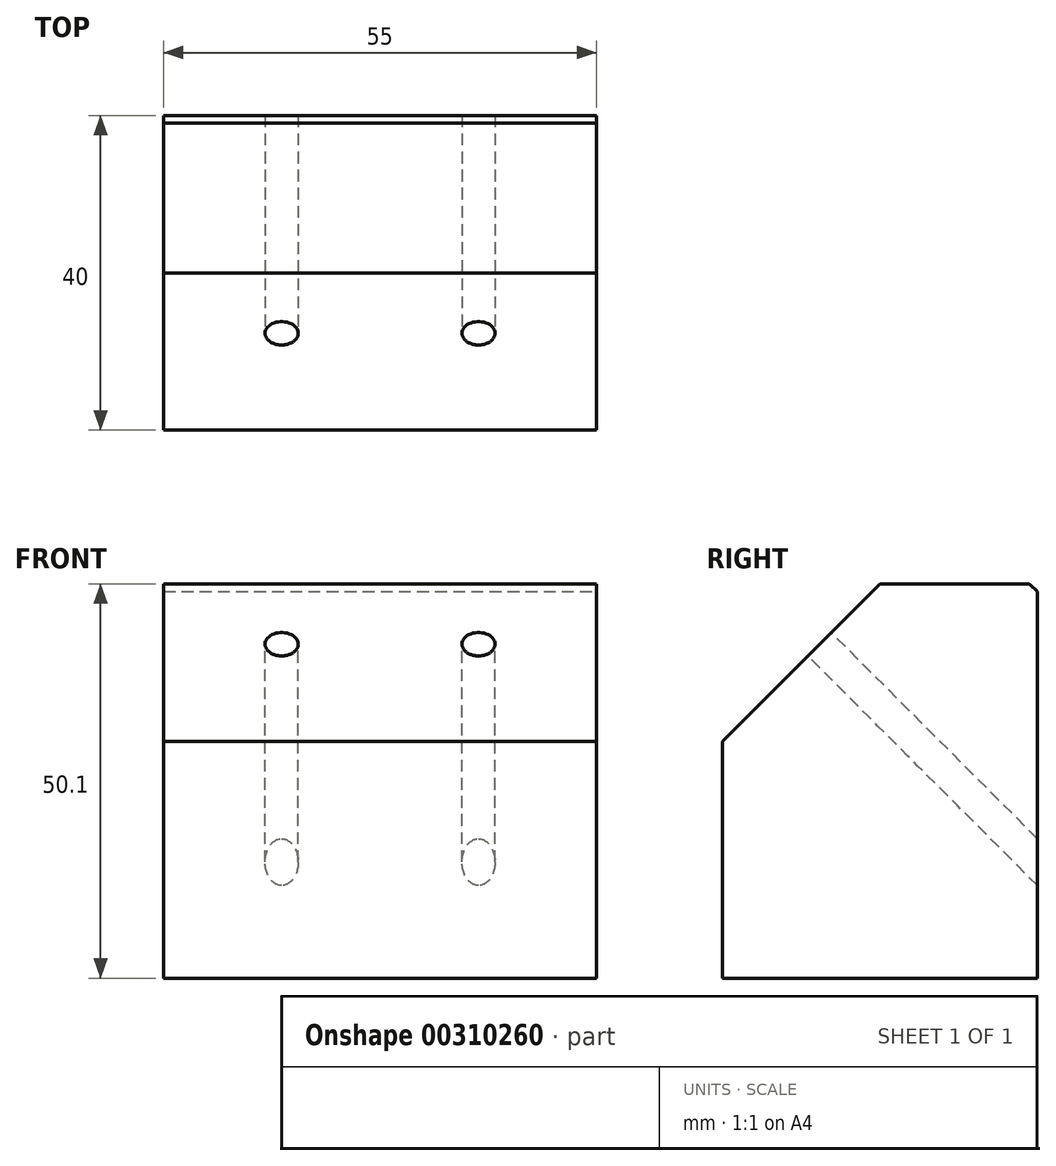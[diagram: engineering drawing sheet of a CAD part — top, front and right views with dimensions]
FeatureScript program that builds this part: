
annotation { "Feature Type Name" : "Feature", "Feature Type Description" : "" }
export const myFeature = defineFeature(function(context is Context, id is Id, definition is map)
    precondition{}
    {
        {
            var Q0;
            Q0=qCreatedBy(makeId("Top.planeOp"),FACE);
            var sketch = newSketch(context, id + "F0", { "sketchPlane" : qUnion([Q0])});
            skLineSegment(sketch, "E0.bottom", {"start": v(0, 0) * mm, "end": v(55, 0) * mm});
            skLineSegment(sketch, "E0.top", {"start": v(0, 40) * mm, "end": v(55, 40) * mm});
            skLineSegment(sketch, "E0.left", {"start": v(0, 0) * mm, "end": v(0, 40) * mm});
            skLineSegment(sketch, "E0.right", {"start": v(55, 0) * mm, "end": v(55, 40) * mm});
            skSolve(sketch);
        }
        {
            var Q0;
            Q0=makeQuery(id+"F0.imprint","IMPRINT",FACE,{"disambiguationData":[TD([[makeQuery(id+"F0.imprint","IMPRINT",EDGE,{"derivedFrom":sQuery(id+"F0.wireOp",EDGE,"E0.bottom")}),1.0]])]});
            extrude(context, id + "F1", {"entities" : qUnion([Q0]), "depth" : 50.1 * mm});
        }
        {
            var Q0;
            Q0=makeQuery(id+"F1.opExtrude","CAP_EDGE",EDGE,{"disambiguationData":[OSD([sQuery(id+"F0.wireOp",EDGE,"E0.bottom")])],"isStart":false});
            chamfer(context, id + "F2", {"entities" : qUnion([Q0]), "width" : 20 * mm, "tangentPropagation" : true});
        }
        {
            var Q0;
            Q0=makeQuery(id+"F2.opChamfer","BLEND_FACE",FACE,{"disambiguationData":[OSD([sQuery(id+"F0.wireOp",EDGE,"E0.bottom")])]});
            var sketch = newSketch(context, id + "F3", { "sketchPlane" : qUnion([Q0])});
            skPoint(sketch, "E1", {"position": v(0, 38.7) * mm});
            skPoint(sketch, "E2", {"position": v(-0.1, 38.7) * mm});
            skPoint(sketch, "E3", {"position": v(15, 38.7) * mm});
            skPoint(sketch, "E4", {"position": v(40, 38.7) * mm});
            skPoint(sketch, "E5", {"position": v(55, 38.7) * mm});
            skSolve(sketch);
        }
        {
            var Q0;
            Q0=sQuery(id+"F3.wireOp",VERTEX,"E4");
            var Q1;
            Q1=sQuery(id+"F3.wireOp",VERTEX,"E3");
            var Q2;
            Q2=makeQuery(id+"F1.opExtrude","SWEPT_BODY",BODY,{"disambiguationData":[OSD([sQuery(id+"F0.wireOp",EDGE,"E0.bottom"),sQuery(id+"F0.wireOp",EDGE,"E0.top"),sQuery(id+"F0.wireOp",EDGE,"E0.left"),sQuery(id+"F0.wireOp",EDGE,"E0.right")])]});
            hole(context, id + "F4", {"style" : HoleStyle.SIMPLE, "endStyle" : HoleEndStyle.THROUGH, "standardTappedOrClearance" : lookupTablePath({ "standard" : "ISO", "engagement" : "75%", "pitch" : "0.8 mm", "size" : "M5", "type" : "Tapped" }), "standardBlindInLast" : lookupTablePath({ "standard" : "ISO", "engagement" : "75%", "pitch" : "0.8 mm", "size" : "M5", "type" : "Tapped" }), "holeDiameter" : 4.2 * mm, "showTappedDepth" : true, "tappedDepth" : 12 * mm, "tapClearance" : 3, "locations" : qUnion([Q0, Q1]), "scope" : qUnion([Q2]), "majorDiameter" : 5 * mm});
        }
        {
            var Q0;
            Q0=makeQuery(id+"F1.opExtrude","CAP_EDGE",EDGE,{"disambiguationData":[OSD([sQuery(id+"F0.wireOp",EDGE,"E0.top")])],"isStart":false});
            chamfer(context, id + "F5", {"entities" : qUnion([Q0]), "width" : 1 * mm, "tangentPropagation" : true});
        }
    });
